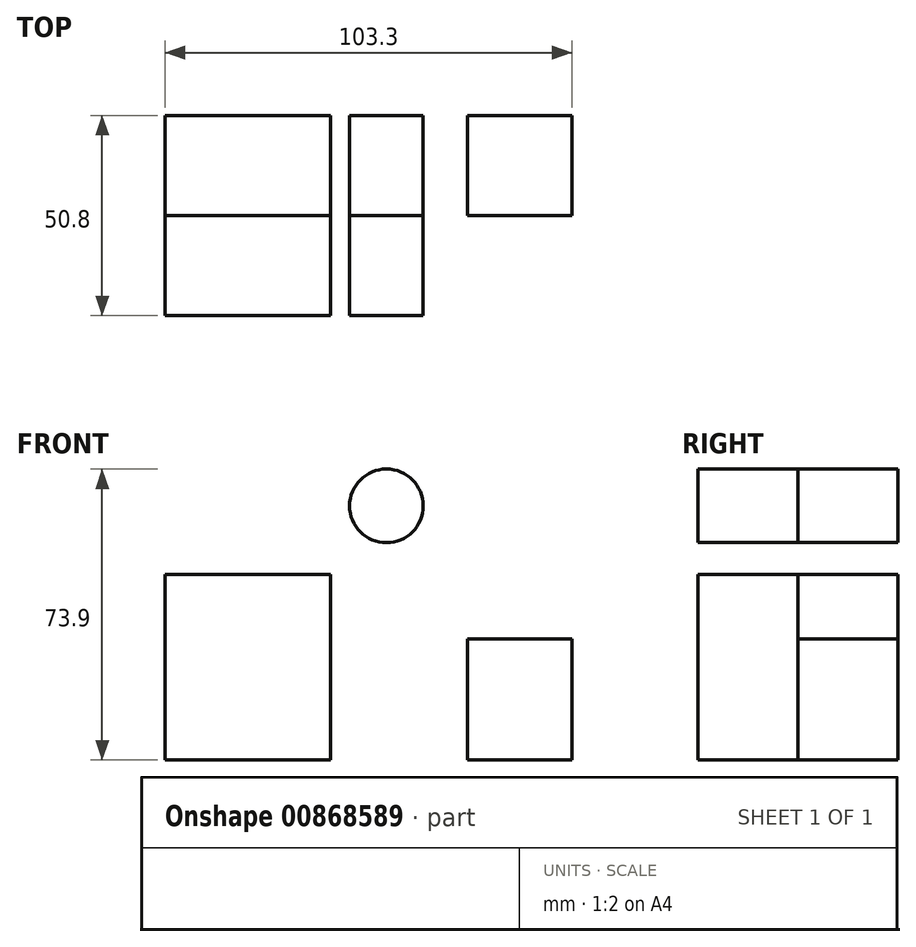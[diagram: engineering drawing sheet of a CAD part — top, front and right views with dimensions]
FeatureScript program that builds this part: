
annotation { "Feature Type Name" : "Feature", "Feature Type Description" : "" }
export const myFeature = defineFeature(function(context is Context, id is Id, definition is map)
    precondition{}
    {
        {
            var Q0;
            Q0=qCreatedBy(makeId("Front.planeOp"),FACE);
            var sketch = newSketch(context, id + "F0", { "sketchPlane" : qUnion([Q0])});
            skLineSegment(sketch, "E0.bottom", {"start": v(-50.23, 27.47) * mm, "end": v(-8.27, 27.47) * mm});
            skLineSegment(sketch, "E0.top", {"start": v(-50.23, -19.65) * mm, "end": v(-8.27, -19.65) * mm});
            skLineSegment(sketch, "E0.left", {"start": v(-50.23, 27.47) * mm, "end": v(-50.23, -19.65) * mm});
            skLineSegment(sketch, "E0.right", {"start": v(-8.27, 27.47) * mm, "end": v(-8.27, -19.65) * mm});
            skLineSegment(sketch, "E1.bottom", {"start": v(26.58, 11.11) * mm, "end": v(53.07, 11.11) * mm});
            skLineSegment(sketch, "E1.top", {"start": v(26.58, -19.65) * mm, "end": v(53.07, -19.65) * mm});
            skLineSegment(sketch, "E1.left", {"start": v(26.58, 11.11) * mm, "end": v(26.58, -19.65) * mm});
            skLineSegment(sketch, "E1.right", {"start": v(53.07, 11.11) * mm, "end": v(53.07, -19.65) * mm});
            skCircle(sketch, "E2", {"center": v(5.96, 44.9) * mm, "radius": 9.35 * mm});
            skSolve(sketch);
        }
        {
            var Q0;
            Q0=makeQuery(id+"F0.imprint","IMPRINT",FACE,{"disambiguationData":[TD([[makeQuery(id+"F0.imprint","IMPRINT",EDGE,{"derivedFrom":sQuery(id+"F0.wireOp",EDGE,"E1.bottom")}),-1.0]])]});
            var Q1;
            Q1=makeQuery(id+"F0.imprint","IMPRINT",FACE,{"disambiguationData":[TD([[makeQuery(id+"F0.imprint","IMPRINT",EDGE,{"derivedFrom":sQuery(id+"F0.wireOp",EDGE,"E0.bottom")}),-1.0]])]});
            var Q2;
            Q2=makeQuery(id+"F0.imprint","IMPRINT",FACE,{"disambiguationData":[TD([[makeQuery(id+"F0.imprint","IMPRINT",EDGE,{"derivedFrom":sQuery(id+"F0.wireOp",EDGE,"E2")}),1.0]])]});
            extrude(context, id + "F1", {"entities" : qUnion([Q0, Q1, Q2]), "depth" : 25.4 * mm, "offsetDistance" : 25.4 * mm});
        }
        {
            var Q0;
            Q0=makeQuery(id+"F1.opExtrude","CAP_FACE",FACE,{"disambiguationData":[OSD([sQuery(id+"F0.wireOp",EDGE,"E0.bottom"),sQuery(id+"F0.wireOp",EDGE,"E0.top"),sQuery(id+"F0.wireOp",EDGE,"E0.left"),sQuery(id+"F0.wireOp",EDGE,"E0.right")])],"isStart":false});
            var Q1;
            Q1=makeQuery(id+"F1.opExtrude","CAP_FACE",FACE,{"disambiguationData":[OSD([sQuery(id+"F0.wireOp",EDGE,"E2")])],"isStart":false});
            extrude(context, id + "F2", {"entities" : qUnion([Q0, Q1]), "depth" : 25.4 * mm, "offsetDistance" : 25.4 * mm});
        }
    });
